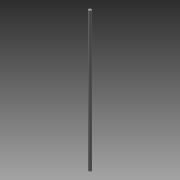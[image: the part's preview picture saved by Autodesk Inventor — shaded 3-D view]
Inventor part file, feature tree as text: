
AUTODESK INVENTOR PART (.ipt)
format: ipt  version: 2013 (Build 170138000, 138)  size: 67,584 bytes
history: native  units: in
note: dims shown in document units (in); Inventor stores cm internally (conversion verified against a paired STEP export)
features: extrude x1, sketch x1
ambient origin geometry x8: Origin, YZ Plane, XZ Plane, XY Plane, X Axis, Y Axis, Z Axis, Center Point
bodies: Solid1 (feature_tree)
feature tree (2):
  extrude  "Extrusion1"  Depth=22.75in TaperAngle=0.0deg
  sketch  "Sketch1"  dims[d0=0.5in d1=22.75in d2=0.0in]
